# Revit family: MHY-20
name_source: partatom
category: Plumbing Fixtures
units: mm (PartAtom-declared; Revit-internal decimal feet)

## family parameters
Classification Number = 23.45.55.21
Cut with Voids When Loaded = No
Enable Cutting in Views = No
Host = Face
Maintain Annotation Orientation = No
Part Type = Normal
Room Calculation Point = No
Round Connector Dimension = Use Diameter
Shared = No

## types (10) — shared parameters
Hydrant Material = Chrome Plated
Manufacturer = MIFAB
Model = MHY-20
URL = www.mifab.com
zero-valued in all types: Default Elevation, WFU

## per-type parameters (varying)
| type | Description | Wall Thikness |
| MHY-20-6 | Encased Non-Freeze Wall Hydrant | 6 " |
| MHY-20-8 | Encased Non-Freeze Wall Hydrant | 8 " |
| MHY-20-10 | Encased Non-Freeze Wall Hydrant | 10 " |
| MHY-20-12 | Encased Non-Freeze Wall Hydrant | 12 " |
| MHY-20-14 | Encased Non-Freeze Wall Hydrant
Encased Non-Freeze Wall Hydrant

Encased Non-Freeze Wall Hydrant | 14 " |
| MHY-20-16 | Encased Non-Freeze Wall Hydrant | 16 " |
| MHY-20-18 | Encased Non-Freeze Wall Hydrant | 18 " |
| MHY-20-20 | Encased Non-Freeze Wall Hydrant | 20 " |
| MHY-20-22 | Encased Non-Freeze Wall Hydrant | 22 " |
| MHY-20-24 | Encased Non-Freeze Wall Hydrant | 24 " |

## geometry (parser evidence)
native form markers: Blend x2, Sweep x2
no freeform markers — native parametric forms only
